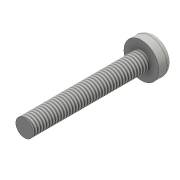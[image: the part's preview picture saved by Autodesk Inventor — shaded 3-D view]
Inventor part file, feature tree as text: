
AUTODESK INVENTOR PART (.ipt)
format: ipt  version: 2016 (Build 200138000, 138)  size: 114,176 bytes
history: native  units: mm
features: extrude x3, sketch x3, fillet x1, thread x1
ambient origin geometry x8: Origin, YZ Plane, XZ Plane, XY Plane, X Axis, Y Axis, Z Axis, Center Point
bodies: Solid1 (feature_tree)
feature tree (8):
  extrude  "Extrusion1"  Depth=2.4mm TaperAngle=0.0deg
  extrude  "Extrusion2"  Depth=0.5mm
  fillet  "Fillet1"  Radius=0.5mm
  extrude  "Extrusion3"  Depth=1.0mm TaperAngle=0.0deg
  thread  "Thread1"  [1 undecoded]
  sketch  "Sketch1"  dims[d0=6.0mm d1=2.4mm d2=0.0mm]
  sketch  "Sketch2"  dims[d5=3.1mm d6=0.5mm d9=0.5mm]
  sketch  "Sketch3"  dims[d10=3.1mm d11=1.0mm d12=0.0mm d13=1.0mm d14=3.0mm d15=20.0mm d16=0.0mm d17=10.0mm d18=0.0mm]
note: 1 required parameter value undecoded (feature->parameter linkage not recoverable at this tier; creation-order binding heuristic only, values carry confidence <= 0.55)
